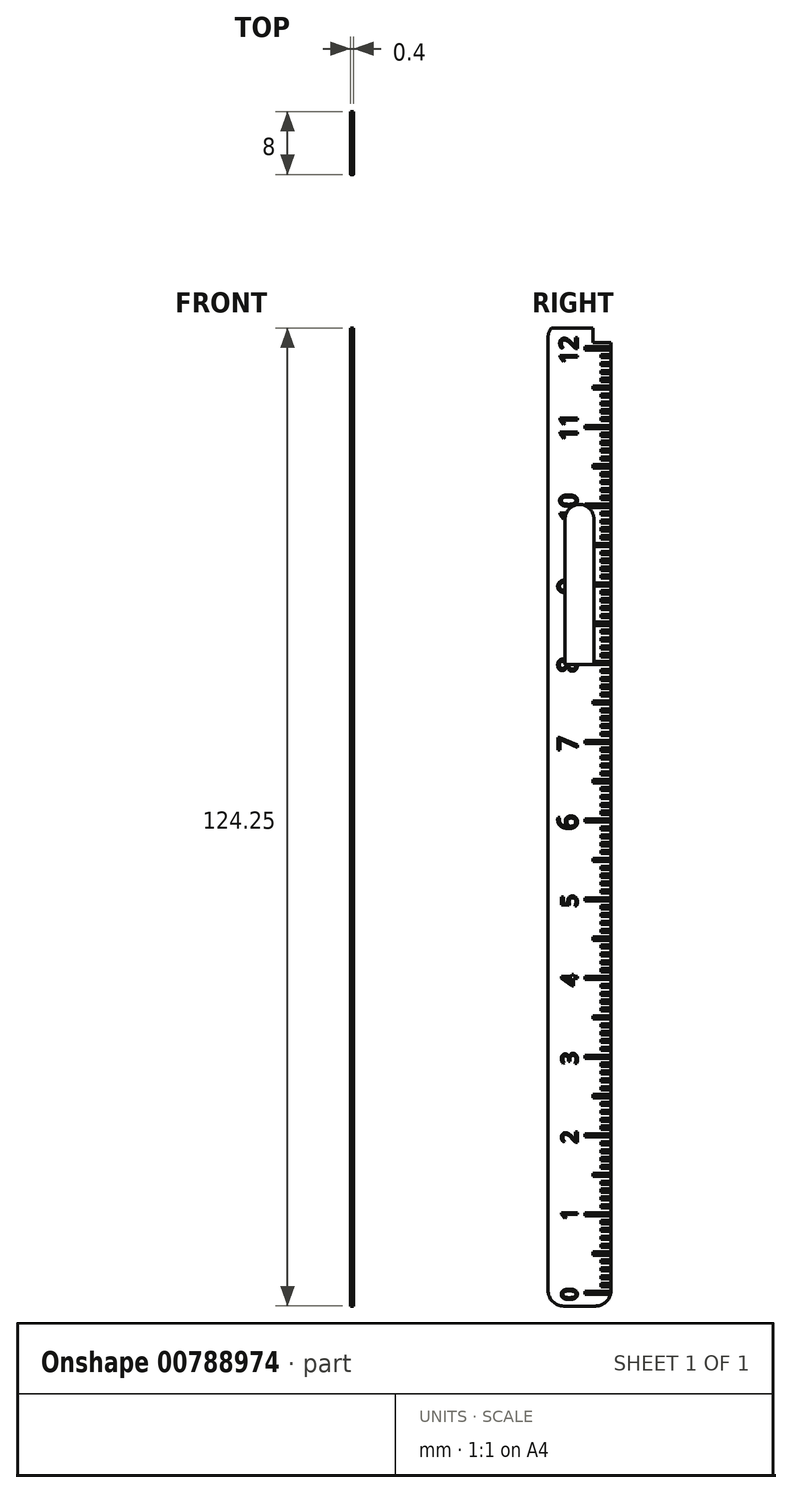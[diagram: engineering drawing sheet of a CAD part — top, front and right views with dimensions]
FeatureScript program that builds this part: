
annotation { "Feature Type Name" : "Feature", "Feature Type Description" : "" }
export const myFeature = defineFeature(function(context is Context, id is Id, definition is map)
    precondition{}
    {
        {
            var Q0;
            Q0=qCreatedBy(makeId("Right.planeOp"),FACE);
            var sketch = newSketch(context, id + "F0", { "sketchPlane" : qUnion([Q0])});
            skLineSegment(sketch, "E0.bottom", {"start": v(-20, 0) * mm, "end": v(-10, 0) * mm});
            skLineSegment(sketch, "E0.top", {"start": v(-20, 160) * mm, "end": v(-10, 160) * mm});
            skLineSegment(sketch, "E0.left", {"start": v(-20, 0) * mm, "end": v(-20, 160) * mm});
            skLineSegment(sketch, "E0.right", {"start": v(-10, 0) * mm, "end": v(-10, 160) * mm});
            skSolve(sketch);
        }
        {
            var Q0;
            Q0=qSketchRegion(id+"F0",true);
            extrude(context, id + "F1", {"entities" : qUnion([Q0]), "depth" : 0.1 * mm, "offsetDistance" : 25 * mm});
        }
        {
            var Q0;
            Q0=qCreatedBy(makeId("Right.planeOp"),FACE);
            var sketch = newSketch(context, id + "F2", { "sketchPlane" : qUnion([Q0])});
            skLineSegment(sketch, "E1", {"start": v(-12, 0) * mm, "end": v(-12, 150) * mm, "construction": true});
            skLineSegment(sketch, "E2", {"start": v(-14, 0) * mm, "end": v(-14, 150) * mm, "construction": true});
            skLineSegment(sketch, "E3", {"start": v(-13, 0) * mm, "end": v(-13, 150) * mm, "construction": true});
            skLineSegment(sketch, "E4.bottom", {"start": v(-14, 10.4) * mm, "end": v(-10, 10.4) * mm});
            skLineSegment(sketch, "E4.top", {"start": v(-14, 10) * mm, "end": v(-10, 10) * mm});
            skLineSegment(sketch, "E4.left", {"start": v(-14, 10) * mm, "end": v(-14, 10.4) * mm});
            skLineSegment(sketch, "E4.right", {"start": v(-10, 10) * mm, "end": v(-10, 10.4) * mm});
            skLineSegment(sketch, "E5.0.1.0", {"start": v(-14, 20.4) * mm, "end": v(-10, 20.4) * mm});
            skLineSegment(sketch, "E5.0.1.1", {"start": v(-14, 20) * mm, "end": v(-10, 20) * mm});
            skLineSegment(sketch, "E5.0.1.2", {"start": v(-14, 20) * mm, "end": v(-14, 20.4) * mm});
            skLineSegment(sketch, "E5.0.1.3", {"start": v(-10, 20) * mm, "end": v(-10, 20.4) * mm});
            skLineSegment(sketch, "E5.0.2.0", {"start": v(-14, 30.4) * mm, "end": v(-10, 30.4) * mm});
            skLineSegment(sketch, "E5.0.2.1", {"start": v(-14, 30) * mm, "end": v(-10, 30) * mm});
            skLineSegment(sketch, "E5.0.2.2", {"start": v(-14, 30) * mm, "end": v(-14, 30.4) * mm});
            skLineSegment(sketch, "E5.0.2.3", {"start": v(-10, 30) * mm, "end": v(-10, 30.4) * mm});
            skLineSegment(sketch, "E5.0.3.0", {"start": v(-14, 40.4) * mm, "end": v(-10, 40.4) * mm});
            skLineSegment(sketch, "E5.0.3.1", {"start": v(-14, 40) * mm, "end": v(-10, 40) * mm});
            skLineSegment(sketch, "E5.0.3.2", {"start": v(-14, 40) * mm, "end": v(-14, 40.4) * mm});
            skLineSegment(sketch, "E5.0.3.3", {"start": v(-10, 40) * mm, "end": v(-10, 40.4) * mm});
            skLineSegment(sketch, "E5.0.4.0", {"start": v(-14, 50.4) * mm, "end": v(-10, 50.4) * mm});
            skLineSegment(sketch, "E5.0.4.1", {"start": v(-14, 50) * mm, "end": v(-10, 50) * mm});
            skLineSegment(sketch, "E5.0.4.2", {"start": v(-14, 50) * mm, "end": v(-14, 50.4) * mm});
            skLineSegment(sketch, "E5.0.4.3", {"start": v(-10, 50) * mm, "end": v(-10, 50.4) * mm});
            skLineSegment(sketch, "E5.0.5.0", {"start": v(-14, 60.4) * mm, "end": v(-10, 60.4) * mm});
            skLineSegment(sketch, "E5.0.5.1", {"start": v(-14, 60) * mm, "end": v(-10, 60) * mm});
            skLineSegment(sketch, "E5.0.5.2", {"start": v(-14, 60) * mm, "end": v(-14, 60.4) * mm});
            skLineSegment(sketch, "E5.0.5.3", {"start": v(-10, 60) * mm, "end": v(-10, 60.4) * mm});
            skLineSegment(sketch, "E5.0.6.0", {"start": v(-14, 70.4) * mm, "end": v(-10, 70.4) * mm});
            skLineSegment(sketch, "E5.0.6.1", {"start": v(-14, 70) * mm, "end": v(-10, 70) * mm});
            skLineSegment(sketch, "E5.0.6.2", {"start": v(-14, 70) * mm, "end": v(-14, 70.4) * mm});
            skLineSegment(sketch, "E5.0.6.3", {"start": v(-10, 70) * mm, "end": v(-10, 70.4) * mm});
            skLineSegment(sketch, "E5.0.7.0", {"start": v(-14, 80.4) * mm, "end": v(-10, 80.4) * mm});
            skLineSegment(sketch, "E5.0.7.1", {"start": v(-14, 80) * mm, "end": v(-10, 80) * mm});
            skLineSegment(sketch, "E5.0.7.2", {"start": v(-14, 80) * mm, "end": v(-14, 80.4) * mm});
            skLineSegment(sketch, "E5.0.7.3", {"start": v(-10, 80) * mm, "end": v(-10, 80.4) * mm});
            skLineSegment(sketch, "E5.0.8.0", {"start": v(-14, 90.4) * mm, "end": v(-10, 90.4) * mm});
            skLineSegment(sketch, "E5.0.8.1", {"start": v(-14, 90) * mm, "end": v(-10, 90) * mm});
            skLineSegment(sketch, "E5.0.8.2", {"start": v(-14, 90) * mm, "end": v(-14, 90.4) * mm});
            skLineSegment(sketch, "E5.0.8.3", {"start": v(-10, 90) * mm, "end": v(-10, 90.4) * mm});
            skLineSegment(sketch, "E5.0.9.0", {"start": v(-14, 100.4) * mm, "end": v(-10, 100.4) * mm});
            skLineSegment(sketch, "E5.0.9.1", {"start": v(-14, 100) * mm, "end": v(-10, 100) * mm});
            skLineSegment(sketch, "E5.0.9.2", {"start": v(-14, 100) * mm, "end": v(-14, 100.4) * mm});
            skLineSegment(sketch, "E5.0.9.3", {"start": v(-10, 100) * mm, "end": v(-10, 100.4) * mm});
            skLineSegment(sketch, "E5.direction2", {"start": v(-14, 10) * mm, "end": v(-14, 20) * mm, "construction": true});
            skLineSegment(sketch, "E6.0.0.10", {"start": v(-14, 110.4) * mm, "end": v(-10, 110.4) * mm});
            skLineSegment(sketch, "E6.3.0.10", {"start": v(-14, 110) * mm, "end": v(-10, 110) * mm});
            skLineSegment(sketch, "E6.6.0.10", {"start": v(-14, 110) * mm, "end": v(-14, 110.4) * mm});
            skLineSegment(sketch, "E6.9.0.10", {"start": v(-10, 110) * mm, "end": v(-10, 110.4) * mm});
            skLineSegment(sketch, "E6.0.0.11", {"start": v(-14, 120.4) * mm, "end": v(-10, 120.4) * mm});
            skLineSegment(sketch, "E6.3.0.11", {"start": v(-14, 120) * mm, "end": v(-10, 120) * mm});
            skLineSegment(sketch, "E6.6.0.11", {"start": v(-14, 120) * mm, "end": v(-14, 120.4) * mm});
            skLineSegment(sketch, "E6.9.0.11", {"start": v(-10, 120) * mm, "end": v(-10, 120.4) * mm});
            skLineSegment(sketch, "E6.0.0.12", {"start": v(-14, 130.4) * mm, "end": v(-10, 130.4) * mm});
            skLineSegment(sketch, "E6.3.0.12", {"start": v(-14, 130) * mm, "end": v(-10, 130) * mm});
            skLineSegment(sketch, "E6.6.0.12", {"start": v(-14, 130) * mm, "end": v(-14, 130.4) * mm});
            skLineSegment(sketch, "E6.9.0.12", {"start": v(-10, 130) * mm, "end": v(-10, 130.4) * mm});
            skLineSegment(sketch, "E6.0.0.13", {"start": v(-14, 140.4) * mm, "end": v(-10, 140.4) * mm});
            skLineSegment(sketch, "E6.3.0.13", {"start": v(-14, 140) * mm, "end": v(-10, 140) * mm});
            skLineSegment(sketch, "E6.6.0.13", {"start": v(-14, 140) * mm, "end": v(-14, 140.4) * mm});
            skLineSegment(sketch, "E6.9.0.13", {"start": v(-10, 140) * mm, "end": v(-10, 140.4) * mm});
            skLineSegment(sketch, "E7.bottom", {"start": v(-10, 15) * mm, "end": v(-13, 15) * mm});
            skLineSegment(sketch, "E7.top", {"start": v(-10, 15.4) * mm, "end": v(-13, 15.4) * mm});
            skLineSegment(sketch, "E7.left", {"start": v(-10, 15) * mm, "end": v(-10, 15.4) * mm});
            skLineSegment(sketch, "E7.right", {"start": v(-13, 15) * mm, "end": v(-13, 15.4) * mm});
            skLineSegment(sketch, "E8", {"start": v(-22.56, 0) * mm, "end": v(-10, 0) * mm, "construction": true});
            skLineSegment(sketch, "E9", {"start": v(-15, 150) * mm, "end": v(-15, 0) * mm, "construction": true});
            skText(sketch, "E10", { "text": "0", "fontName": "OpenSans-Regular.ttf"});
            skText(sketch, "E11", { "text": "1\n", "fontName": "OpenSans-Regular.ttf"});
            skText(sketch, "E12", { "text": "2", "fontName": "OpenSans-Regular.ttf"});
            skText(sketch, "E13", { "text": "3", "fontName": "OpenSans-Regular.ttf"});
            skText(sketch, "E14", { "text": "4", "fontName": "OpenSans-Regular.ttf"});
            skText(sketch, "E15", { "text": "5", "fontName": "OpenSans-Regular.ttf"});
            skText(sketch, "E16", { "text": "6", "fontName": "OpenSans-Regular.ttf"});
            skText(sketch, "E17", { "text": "7", "fontName": "OpenSans-Regular.ttf"});
            skText(sketch, "E18", { "text": "8", "fontName": "OpenSans-Regular.ttf"});
            skText(sketch, "E19", { "text": "9", "fontName": "OpenSans-Regular.ttf"});
            skText(sketch, "E20", { "text": "10", "fontName": "OpenSans-Regular.ttf"});
            skText(sketch, "E21", { "text": "11", "fontName": "OpenSans-Regular.ttf"});
            skText(sketch, "E22", { "text": "12", "fontName": "OpenSans-Regular.ttf"});
            skText(sketch, "E23", { "text": "13", "fontName": "OpenSans-Regular.ttf"});
            skLineSegment(sketch, "E24.bottom", {"start": v(-12, 11) * mm, "end": v(-10, 11) * mm});
            skLineSegment(sketch, "E24.top", {"start": v(-12, 11.4) * mm, "end": v(-10, 11.4) * mm});
            skLineSegment(sketch, "E24.left", {"start": v(-12, 11) * mm, "end": v(-12, 11.4) * mm});
            skLineSegment(sketch, "E24.right", {"start": v(-10, 11) * mm, "end": v(-10, 11.4) * mm});
            skLineSegment(sketch, "E25.bottom", {"start": v(-12, 12) * mm, "end": v(-10, 12) * mm});
            skLineSegment(sketch, "E25.top", {"start": v(-12, 12.4) * mm, "end": v(-10, 12.4) * mm});
            skLineSegment(sketch, "E25.left", {"start": v(-12, 12) * mm, "end": v(-12, 12.4) * mm});
            skLineSegment(sketch, "E25.right", {"start": v(-10, 12) * mm, "end": v(-10, 12.4) * mm});
            skLineSegment(sketch, "E26.bottom", {"start": v(-12, 13) * mm, "end": v(-10, 13) * mm});
            skLineSegment(sketch, "E26.top", {"start": v(-12, 13.4) * mm, "end": v(-10, 13.4) * mm});
            skLineSegment(sketch, "E26.left", {"start": v(-12, 13) * mm, "end": v(-12, 13.4) * mm});
            skLineSegment(sketch, "E26.right", {"start": v(-10, 13) * mm, "end": v(-10, 13.4) * mm});
            skLineSegment(sketch, "E27.bottom", {"start": v(-12, 14) * mm, "end": v(-10, 14) * mm});
            skLineSegment(sketch, "E27.top", {"start": v(-12, 14.4) * mm, "end": v(-10, 14.4) * mm});
            skLineSegment(sketch, "E27.left", {"start": v(-12, 14) * mm, "end": v(-12, 14.4) * mm});
            skLineSegment(sketch, "E27.right", {"start": v(-10, 14) * mm, "end": v(-10, 14.4) * mm});
            skLineSegment(sketch, "E28.bottom", {"start": v(-12, 16) * mm, "end": v(-10, 16) * mm});
            skLineSegment(sketch, "E28.top", {"start": v(-12, 16.4) * mm, "end": v(-10, 16.4) * mm});
            skLineSegment(sketch, "E28.left", {"start": v(-12, 16) * mm, "end": v(-12, 16.4) * mm});
            skLineSegment(sketch, "E28.right", {"start": v(-10, 16) * mm, "end": v(-10, 16.4) * mm});
            skLineSegment(sketch, "E29.bottom", {"start": v(-12, 17) * mm, "end": v(-10, 17) * mm});
            skLineSegment(sketch, "E29.top", {"start": v(-12, 17.4) * mm, "end": v(-10, 17.4) * mm});
            skLineSegment(sketch, "E29.left", {"start": v(-12, 17) * mm, "end": v(-12, 17.4) * mm});
            skLineSegment(sketch, "E29.right", {"start": v(-10, 17) * mm, "end": v(-10, 17.4) * mm});
            skLineSegment(sketch, "E30.bottom", {"start": v(-12, 18) * mm, "end": v(-10, 18) * mm});
            skLineSegment(sketch, "E30.top", {"start": v(-12, 18.4) * mm, "end": v(-10, 18.4) * mm});
            skLineSegment(sketch, "E30.left", {"start": v(-12, 18) * mm, "end": v(-12, 18.4) * mm});
            skLineSegment(sketch, "E30.right", {"start": v(-10, 18) * mm, "end": v(-10, 18.4) * mm});
            skLineSegment(sketch, "E31.bottom", {"start": v(-12, 19) * mm, "end": v(-10, 19) * mm});
            skLineSegment(sketch, "E31.top", {"start": v(-12, 19.4) * mm, "end": v(-10, 19.4) * mm});
            skLineSegment(sketch, "E31.left", {"start": v(-12, 19) * mm, "end": v(-12, 19.4) * mm});
            skLineSegment(sketch, "E31.right", {"start": v(-10, 19) * mm, "end": v(-10, 19.4) * mm});
            skLineSegment(sketch, "E32.0.1.0", {"start": v(-12, 22) * mm, "end": v(-10, 22) * mm});
            skLineSegment(sketch, "E32.0.1.1", {"start": v(-12, 21.4) * mm, "end": v(-10, 21.4) * mm});
            skLineSegment(sketch, "E32.0.1.2", {"start": v(-12, 23.4) * mm, "end": v(-10, 23.4) * mm});
            skLineSegment(sketch, "E32.0.1.3", {"start": v(-12, 28.4) * mm, "end": v(-10, 28.4) * mm});
            skLineSegment(sketch, "E32.0.1.4", {"start": v(-12, 22.4) * mm, "end": v(-10, 22.4) * mm});
            skLineSegment(sketch, "E32.0.1.5", {"start": v(-12, 23) * mm, "end": v(-10, 23) * mm});
            skLineSegment(sketch, "E32.0.1.6", {"start": v(-10, 25.4) * mm, "end": v(-13, 25.4) * mm});
            skLineSegment(sketch, "E32.0.1.7", {"start": v(-12, 29) * mm, "end": v(-10, 29) * mm});
            skLineSegment(sketch, "E32.0.1.8", {"start": v(-12, 29.4) * mm, "end": v(-10, 29.4) * mm});
            skLineSegment(sketch, "E32.0.1.9", {"start": v(-12, 24.4) * mm, "end": v(-10, 24.4) * mm});
            skLineSegment(sketch, "E32.0.1.10", {"start": v(-12, 28) * mm, "end": v(-10, 28) * mm});
            skLineSegment(sketch, "E32.0.1.11", {"start": v(-12, 26) * mm, "end": v(-10, 26) * mm});
            skLineSegment(sketch, "E32.0.1.12", {"start": v(-12, 27) * mm, "end": v(-10, 27) * mm});
            skLineSegment(sketch, "E32.0.1.13", {"start": v(-12, 26.4) * mm, "end": v(-10, 26.4) * mm});
            skLineSegment(sketch, "E32.0.1.14", {"start": v(-12, 21) * mm, "end": v(-10, 21) * mm});
            skLineSegment(sketch, "E32.0.1.15", {"start": v(-10, 25) * mm, "end": v(-13, 25) * mm});
            skLineSegment(sketch, "E32.0.1.16", {"start": v(-12, 10) * mm, "end": v(-12, 160) * mm, "construction": true});
            skLineSegment(sketch, "E32.0.1.17", {"start": v(-13, 10) * mm, "end": v(-13, 160) * mm, "construction": true});
            skLineSegment(sketch, "E32.0.1.18", {"start": v(-12, 24) * mm, "end": v(-10, 24) * mm});
            skLineSegment(sketch, "E32.0.1.19", {"start": v(-12, 27.4) * mm, "end": v(-10, 27.4) * mm});
            skLineSegment(sketch, "E32.0.1.20", {"start": v(-12, 21) * mm, "end": v(-12, 21.4) * mm});
            skLineSegment(sketch, "E32.0.1.21", {"start": v(-10, 24) * mm, "end": v(-10, 24.4) * mm});
            skLineSegment(sketch, "E32.0.1.22", {"start": v(-10, 27) * mm, "end": v(-10, 27.4) * mm});
            skLineSegment(sketch, "E32.0.1.23", {"start": v(-12, 29) * mm, "end": v(-12, 29.4) * mm});
            skLineSegment(sketch, "E32.0.1.24", {"start": v(-10, 25) * mm, "end": v(-10, 25.4) * mm});
            skLineSegment(sketch, "E32.0.1.25", {"start": v(-12, 24) * mm, "end": v(-12, 24.4) * mm});
            skLineSegment(sketch, "E32.0.1.26", {"start": v(-12, 26) * mm, "end": v(-12, 26.4) * mm});
            skLineSegment(sketch, "E32.0.1.27", {"start": v(-10, 28) * mm, "end": v(-10, 28.4) * mm});
            skLineSegment(sketch, "E32.0.1.28", {"start": v(-12, 28) * mm, "end": v(-12, 28.4) * mm});
            skLineSegment(sketch, "E32.0.1.29", {"start": v(-10, 21) * mm, "end": v(-10, 21.4) * mm});
            skLineSegment(sketch, "E32.0.1.30", {"start": v(-10, 26) * mm, "end": v(-10, 26.4) * mm});
            skLineSegment(sketch, "E32.0.1.31", {"start": v(-10, 29) * mm, "end": v(-10, 29.4) * mm});
            skLineSegment(sketch, "E32.0.1.32", {"start": v(-12, 22) * mm, "end": v(-12, 22.4) * mm});
            skLineSegment(sketch, "E32.0.1.33", {"start": v(-10, 23) * mm, "end": v(-10, 23.4) * mm});
            skLineSegment(sketch, "E32.0.1.34", {"start": v(-13, 25) * mm, "end": v(-13, 25.4) * mm});
            skLineSegment(sketch, "E32.0.1.35", {"start": v(-10, 22) * mm, "end": v(-10, 22.4) * mm});
            skLineSegment(sketch, "E32.0.1.36", {"start": v(-12, 27) * mm, "end": v(-12, 27.4) * mm});
            skLineSegment(sketch, "E32.0.1.37", {"start": v(-12, 23) * mm, "end": v(-12, 23.4) * mm});
            skLineSegment(sketch, "E32.0.2.0", {"start": v(-12, 32) * mm, "end": v(-10, 32) * mm});
            skLineSegment(sketch, "E32.0.2.1", {"start": v(-12, 31.4) * mm, "end": v(-10, 31.4) * mm});
            skLineSegment(sketch, "E32.0.2.2", {"start": v(-12, 33.4) * mm, "end": v(-10, 33.4) * mm});
            skLineSegment(sketch, "E32.0.2.3", {"start": v(-12, 38.4) * mm, "end": v(-10, 38.4) * mm});
            skLineSegment(sketch, "E32.0.2.4", {"start": v(-12, 32.4) * mm, "end": v(-10, 32.4) * mm});
            skLineSegment(sketch, "E32.0.2.5", {"start": v(-12, 33) * mm, "end": v(-10, 33) * mm});
            skLineSegment(sketch, "E32.0.2.6", {"start": v(-10, 35.4) * mm, "end": v(-13, 35.4) * mm});
            skLineSegment(sketch, "E32.0.2.7", {"start": v(-12, 39) * mm, "end": v(-10, 39) * mm});
            skLineSegment(sketch, "E32.0.2.8", {"start": v(-12, 39.4) * mm, "end": v(-10, 39.4) * mm});
            skLineSegment(sketch, "E32.0.2.9", {"start": v(-12, 34.4) * mm, "end": v(-10, 34.4) * mm});
            skLineSegment(sketch, "E32.0.2.10", {"start": v(-12, 38) * mm, "end": v(-10, 38) * mm});
            skLineSegment(sketch, "E32.0.2.11", {"start": v(-12, 36) * mm, "end": v(-10, 36) * mm});
            skLineSegment(sketch, "E32.0.2.12", {"start": v(-12, 37) * mm, "end": v(-10, 37) * mm});
            skLineSegment(sketch, "E32.0.2.13", {"start": v(-12, 36.4) * mm, "end": v(-10, 36.4) * mm});
            skLineSegment(sketch, "E32.0.2.14", {"start": v(-12, 31) * mm, "end": v(-10, 31) * mm});
            skLineSegment(sketch, "E32.0.2.15", {"start": v(-10, 35) * mm, "end": v(-13, 35) * mm});
            skLineSegment(sketch, "E32.0.2.16", {"start": v(-12, 20) * mm, "end": v(-12, 170) * mm, "construction": true});
            skLineSegment(sketch, "E32.0.2.17", {"start": v(-13, 20) * mm, "end": v(-13, 170) * mm, "construction": true});
            skLineSegment(sketch, "E32.0.2.18", {"start": v(-12, 34) * mm, "end": v(-10, 34) * mm});
            skLineSegment(sketch, "E32.0.2.19", {"start": v(-12, 37.4) * mm, "end": v(-10, 37.4) * mm});
            skLineSegment(sketch, "E32.0.2.20", {"start": v(-12, 31) * mm, "end": v(-12, 31.4) * mm});
            skLineSegment(sketch, "E32.0.2.21", {"start": v(-10, 34) * mm, "end": v(-10, 34.4) * mm});
            skLineSegment(sketch, "E32.0.2.22", {"start": v(-10, 37) * mm, "end": v(-10, 37.4) * mm});
            skLineSegment(sketch, "E32.0.2.23", {"start": v(-12, 39) * mm, "end": v(-12, 39.4) * mm});
            skLineSegment(sketch, "E32.0.2.24", {"start": v(-10, 35) * mm, "end": v(-10, 35.4) * mm});
            skLineSegment(sketch, "E32.0.2.25", {"start": v(-12, 34) * mm, "end": v(-12, 34.4) * mm});
            skLineSegment(sketch, "E32.0.2.26", {"start": v(-12, 36) * mm, "end": v(-12, 36.4) * mm});
            skLineSegment(sketch, "E32.0.2.27", {"start": v(-10, 38) * mm, "end": v(-10, 38.4) * mm});
            skLineSegment(sketch, "E32.0.2.28", {"start": v(-12, 38) * mm, "end": v(-12, 38.4) * mm});
            skLineSegment(sketch, "E32.0.2.29", {"start": v(-10, 31) * mm, "end": v(-10, 31.4) * mm});
            skLineSegment(sketch, "E32.0.2.30", {"start": v(-10, 36) * mm, "end": v(-10, 36.4) * mm});
            skLineSegment(sketch, "E32.0.2.31", {"start": v(-10, 39) * mm, "end": v(-10, 39.4) * mm});
            skLineSegment(sketch, "E32.0.2.32", {"start": v(-12, 32) * mm, "end": v(-12, 32.4) * mm});
            skLineSegment(sketch, "E32.0.2.33", {"start": v(-10, 33) * mm, "end": v(-10, 33.4) * mm});
            skLineSegment(sketch, "E32.0.2.34", {"start": v(-13, 35) * mm, "end": v(-13, 35.4) * mm});
            skLineSegment(sketch, "E32.0.2.35", {"start": v(-10, 32) * mm, "end": v(-10, 32.4) * mm});
            skLineSegment(sketch, "E32.0.2.36", {"start": v(-12, 37) * mm, "end": v(-12, 37.4) * mm});
            skLineSegment(sketch, "E32.0.2.37", {"start": v(-12, 33) * mm, "end": v(-12, 33.4) * mm});
            skLineSegment(sketch, "E32.0.3.0", {"start": v(-12, 42) * mm, "end": v(-10, 42) * mm});
            skLineSegment(sketch, "E32.0.3.1", {"start": v(-12, 41.4) * mm, "end": v(-10, 41.4) * mm});
            skLineSegment(sketch, "E32.0.3.2", {"start": v(-12, 43.4) * mm, "end": v(-10, 43.4) * mm});
            skLineSegment(sketch, "E32.0.3.3", {"start": v(-12, 48.4) * mm, "end": v(-10, 48.4) * mm});
            skLineSegment(sketch, "E32.0.3.4", {"start": v(-12, 42.4) * mm, "end": v(-10, 42.4) * mm});
            skLineSegment(sketch, "E32.0.3.5", {"start": v(-12, 43) * mm, "end": v(-10, 43) * mm});
            skLineSegment(sketch, "E32.0.3.6", {"start": v(-10, 45.4) * mm, "end": v(-13, 45.4) * mm});
            skLineSegment(sketch, "E32.0.3.7", {"start": v(-12, 49) * mm, "end": v(-10, 49) * mm});
            skLineSegment(sketch, "E32.0.3.8", {"start": v(-12, 49.4) * mm, "end": v(-10, 49.4) * mm});
            skLineSegment(sketch, "E32.0.3.9", {"start": v(-12, 44.4) * mm, "end": v(-10, 44.4) * mm});
            skLineSegment(sketch, "E32.0.3.10", {"start": v(-12, 48) * mm, "end": v(-10, 48) * mm});
            skLineSegment(sketch, "E32.0.3.11", {"start": v(-12, 46) * mm, "end": v(-10, 46) * mm});
            skLineSegment(sketch, "E32.0.3.12", {"start": v(-12, 47) * mm, "end": v(-10, 47) * mm});
            skLineSegment(sketch, "E32.0.3.13", {"start": v(-12, 46.4) * mm, "end": v(-10, 46.4) * mm});
            skLineSegment(sketch, "E32.0.3.14", {"start": v(-12, 41) * mm, "end": v(-10, 41) * mm});
            skLineSegment(sketch, "E32.0.3.15", {"start": v(-10, 45) * mm, "end": v(-13, 45) * mm});
            skLineSegment(sketch, "E32.0.3.16", {"start": v(-12, 30) * mm, "end": v(-12, 180) * mm, "construction": true});
            skLineSegment(sketch, "E32.0.3.17", {"start": v(-13, 30) * mm, "end": v(-13, 180) * mm, "construction": true});
            skLineSegment(sketch, "E32.0.3.18", {"start": v(-12, 44) * mm, "end": v(-10, 44) * mm});
            skLineSegment(sketch, "E32.0.3.19", {"start": v(-12, 47.4) * mm, "end": v(-10, 47.4) * mm});
            skLineSegment(sketch, "E32.0.3.20", {"start": v(-12, 41) * mm, "end": v(-12, 41.4) * mm});
            skLineSegment(sketch, "E32.0.3.21", {"start": v(-10, 44) * mm, "end": v(-10, 44.4) * mm});
            skLineSegment(sketch, "E32.0.3.22", {"start": v(-10, 47) * mm, "end": v(-10, 47.4) * mm});
            skLineSegment(sketch, "E32.0.3.23", {"start": v(-12, 49) * mm, "end": v(-12, 49.4) * mm});
            skLineSegment(sketch, "E32.0.3.24", {"start": v(-10, 45) * mm, "end": v(-10, 45.4) * mm});
            skLineSegment(sketch, "E32.0.3.25", {"start": v(-12, 44) * mm, "end": v(-12, 44.4) * mm});
            skLineSegment(sketch, "E32.0.3.26", {"start": v(-12, 46) * mm, "end": v(-12, 46.4) * mm});
            skLineSegment(sketch, "E32.0.3.27", {"start": v(-10, 48) * mm, "end": v(-10, 48.4) * mm});
            skLineSegment(sketch, "E32.0.3.28", {"start": v(-12, 48) * mm, "end": v(-12, 48.4) * mm});
            skLineSegment(sketch, "E32.0.3.29", {"start": v(-10, 41) * mm, "end": v(-10, 41.4) * mm});
            skLineSegment(sketch, "E32.0.3.30", {"start": v(-10, 46) * mm, "end": v(-10, 46.4) * mm});
            skLineSegment(sketch, "E32.0.3.31", {"start": v(-10, 49) * mm, "end": v(-10, 49.4) * mm});
            skLineSegment(sketch, "E32.0.3.32", {"start": v(-12, 42) * mm, "end": v(-12, 42.4) * mm});
            skLineSegment(sketch, "E32.0.3.33", {"start": v(-10, 43) * mm, "end": v(-10, 43.4) * mm});
            skLineSegment(sketch, "E32.0.3.34", {"start": v(-13, 45) * mm, "end": v(-13, 45.4) * mm});
            skLineSegment(sketch, "E32.0.3.35", {"start": v(-10, 42) * mm, "end": v(-10, 42.4) * mm});
            skLineSegment(sketch, "E32.0.3.36", {"start": v(-12, 47) * mm, "end": v(-12, 47.4) * mm});
            skLineSegment(sketch, "E32.0.3.37", {"start": v(-12, 43) * mm, "end": v(-12, 43.4) * mm});
            skLineSegment(sketch, "E32.0.4.0", {"start": v(-12, 52) * mm, "end": v(-10, 52) * mm});
            skLineSegment(sketch, "E32.0.4.1", {"start": v(-12, 51.4) * mm, "end": v(-10, 51.4) * mm});
            skLineSegment(sketch, "E32.0.4.2", {"start": v(-12, 53.4) * mm, "end": v(-10, 53.4) * mm});
            skLineSegment(sketch, "E32.0.4.3", {"start": v(-12, 58.4) * mm, "end": v(-10, 58.4) * mm});
            skLineSegment(sketch, "E32.0.4.4", {"start": v(-12, 52.4) * mm, "end": v(-10, 52.4) * mm});
            skLineSegment(sketch, "E32.0.4.5", {"start": v(-12, 53) * mm, "end": v(-10, 53) * mm});
            skLineSegment(sketch, "E32.0.4.6", {"start": v(-10, 55.4) * mm, "end": v(-13, 55.4) * mm});
            skLineSegment(sketch, "E32.0.4.7", {"start": v(-12, 59) * mm, "end": v(-10, 59) * mm});
            skLineSegment(sketch, "E32.0.4.8", {"start": v(-12, 59.4) * mm, "end": v(-10, 59.4) * mm});
            skLineSegment(sketch, "E32.0.4.9", {"start": v(-12, 54.4) * mm, "end": v(-10, 54.4) * mm});
            skLineSegment(sketch, "E32.0.4.10", {"start": v(-12, 58) * mm, "end": v(-10, 58) * mm});
            skLineSegment(sketch, "E32.0.4.11", {"start": v(-12, 56) * mm, "end": v(-10, 56) * mm});
            skLineSegment(sketch, "E32.0.4.12", {"start": v(-12, 57) * mm, "end": v(-10, 57) * mm});
            skLineSegment(sketch, "E32.0.4.13", {"start": v(-12, 56.4) * mm, "end": v(-10, 56.4) * mm});
            skLineSegment(sketch, "E32.0.4.14", {"start": v(-12, 51) * mm, "end": v(-10, 51) * mm});
            skLineSegment(sketch, "E32.0.4.15", {"start": v(-10, 55) * mm, "end": v(-13, 55) * mm});
            skLineSegment(sketch, "E32.0.4.16", {"start": v(-12, 40) * mm, "end": v(-12, 190) * mm, "construction": true});
            skLineSegment(sketch, "E32.0.4.17", {"start": v(-13, 40) * mm, "end": v(-13, 190) * mm, "construction": true});
            skLineSegment(sketch, "E32.0.4.18", {"start": v(-12, 54) * mm, "end": v(-10, 54) * mm});
            skLineSegment(sketch, "E32.0.4.19", {"start": v(-12, 57.4) * mm, "end": v(-10, 57.4) * mm});
            skLineSegment(sketch, "E32.0.4.20", {"start": v(-12, 51) * mm, "end": v(-12, 51.4) * mm});
            skLineSegment(sketch, "E32.0.4.21", {"start": v(-10, 54) * mm, "end": v(-10, 54.4) * mm});
            skLineSegment(sketch, "E32.0.4.22", {"start": v(-10, 57) * mm, "end": v(-10, 57.4) * mm});
            skLineSegment(sketch, "E32.0.4.23", {"start": v(-12, 59) * mm, "end": v(-12, 59.4) * mm});
            skLineSegment(sketch, "E32.0.4.24", {"start": v(-10, 55) * mm, "end": v(-10, 55.4) * mm});
            skLineSegment(sketch, "E32.0.4.25", {"start": v(-12, 54) * mm, "end": v(-12, 54.4) * mm});
            skLineSegment(sketch, "E32.0.4.26", {"start": v(-12, 56) * mm, "end": v(-12, 56.4) * mm});
            skLineSegment(sketch, "E32.0.4.27", {"start": v(-10, 58) * mm, "end": v(-10, 58.4) * mm});
            skLineSegment(sketch, "E32.0.4.28", {"start": v(-12, 58) * mm, "end": v(-12, 58.4) * mm});
            skLineSegment(sketch, "E32.0.4.29", {"start": v(-10, 51) * mm, "end": v(-10, 51.4) * mm});
            skLineSegment(sketch, "E32.0.4.30", {"start": v(-10, 56) * mm, "end": v(-10, 56.4) * mm});
            skLineSegment(sketch, "E32.0.4.31", {"start": v(-10, 59) * mm, "end": v(-10, 59.4) * mm});
            skLineSegment(sketch, "E32.0.4.32", {"start": v(-12, 52) * mm, "end": v(-12, 52.4) * mm});
            skLineSegment(sketch, "E32.0.4.33", {"start": v(-10, 53) * mm, "end": v(-10, 53.4) * mm});
            skLineSegment(sketch, "E32.0.4.34", {"start": v(-13, 55) * mm, "end": v(-13, 55.4) * mm});
            skLineSegment(sketch, "E32.0.4.35", {"start": v(-10, 52) * mm, "end": v(-10, 52.4) * mm});
            skLineSegment(sketch, "E32.0.4.36", {"start": v(-12, 57) * mm, "end": v(-12, 57.4) * mm});
            skLineSegment(sketch, "E32.0.4.37", {"start": v(-12, 53) * mm, "end": v(-12, 53.4) * mm});
            skLineSegment(sketch, "E32.0.5.0", {"start": v(-12, 62) * mm, "end": v(-10, 62) * mm});
            skLineSegment(sketch, "E32.0.5.1", {"start": v(-12, 61.4) * mm, "end": v(-10, 61.4) * mm});
            skLineSegment(sketch, "E32.0.5.2", {"start": v(-12, 63.4) * mm, "end": v(-10, 63.4) * mm});
            skLineSegment(sketch, "E32.0.5.3", {"start": v(-12, 68.4) * mm, "end": v(-10, 68.4) * mm});
            skLineSegment(sketch, "E32.0.5.4", {"start": v(-12, 62.4) * mm, "end": v(-10, 62.4) * mm});
            skLineSegment(sketch, "E32.0.5.5", {"start": v(-12, 63) * mm, "end": v(-10, 63) * mm});
            skLineSegment(sketch, "E32.0.5.6", {"start": v(-10, 65.4) * mm, "end": v(-13, 65.4) * mm});
            skLineSegment(sketch, "E32.0.5.7", {"start": v(-12, 69) * mm, "end": v(-10, 69) * mm});
            skLineSegment(sketch, "E32.0.5.8", {"start": v(-12, 69.4) * mm, "end": v(-10, 69.4) * mm});
            skLineSegment(sketch, "E32.0.5.9", {"start": v(-12, 64.4) * mm, "end": v(-10, 64.4) * mm});
            skLineSegment(sketch, "E32.0.5.10", {"start": v(-12, 68) * mm, "end": v(-10, 68) * mm});
            skLineSegment(sketch, "E32.0.5.11", {"start": v(-12, 66) * mm, "end": v(-10, 66) * mm});
            skLineSegment(sketch, "E32.0.5.12", {"start": v(-12, 67) * mm, "end": v(-10, 67) * mm});
            skLineSegment(sketch, "E32.0.5.13", {"start": v(-12, 66.4) * mm, "end": v(-10, 66.4) * mm});
            skLineSegment(sketch, "E32.0.5.14", {"start": v(-12, 61) * mm, "end": v(-10, 61) * mm});
            skLineSegment(sketch, "E32.0.5.15", {"start": v(-10, 65) * mm, "end": v(-13, 65) * mm});
            skLineSegment(sketch, "E32.0.5.16", {"start": v(-12, 50) * mm, "end": v(-12, 200) * mm, "construction": true});
            skLineSegment(sketch, "E32.0.5.17", {"start": v(-13, 50) * mm, "end": v(-13, 200) * mm, "construction": true});
            skLineSegment(sketch, "E32.0.5.18", {"start": v(-12, 64) * mm, "end": v(-10, 64) * mm});
            skLineSegment(sketch, "E32.0.5.19", {"start": v(-12, 67.4) * mm, "end": v(-10, 67.4) * mm});
            skLineSegment(sketch, "E32.0.5.20", {"start": v(-12, 61) * mm, "end": v(-12, 61.4) * mm});
            skLineSegment(sketch, "E32.0.5.21", {"start": v(-10, 64) * mm, "end": v(-10, 64.4) * mm});
            skLineSegment(sketch, "E32.0.5.22", {"start": v(-10, 67) * mm, "end": v(-10, 67.4) * mm});
            skLineSegment(sketch, "E32.0.5.23", {"start": v(-12, 69) * mm, "end": v(-12, 69.4) * mm});
            skLineSegment(sketch, "E32.0.5.24", {"start": v(-10, 65) * mm, "end": v(-10, 65.4) * mm});
            skLineSegment(sketch, "E32.0.5.25", {"start": v(-12, 64) * mm, "end": v(-12, 64.4) * mm});
            skLineSegment(sketch, "E32.0.5.26", {"start": v(-12, 66) * mm, "end": v(-12, 66.4) * mm});
            skLineSegment(sketch, "E32.0.5.27", {"start": v(-10, 68) * mm, "end": v(-10, 68.4) * mm});
            skLineSegment(sketch, "E32.0.5.28", {"start": v(-12, 68) * mm, "end": v(-12, 68.4) * mm});
            skLineSegment(sketch, "E32.0.5.29", {"start": v(-10, 61) * mm, "end": v(-10, 61.4) * mm});
            skLineSegment(sketch, "E32.0.5.30", {"start": v(-10, 66) * mm, "end": v(-10, 66.4) * mm});
            skLineSegment(sketch, "E32.0.5.31", {"start": v(-10, 69) * mm, "end": v(-10, 69.4) * mm});
            skLineSegment(sketch, "E32.0.5.32", {"start": v(-12, 62) * mm, "end": v(-12, 62.4) * mm});
            skLineSegment(sketch, "E32.0.5.33", {"start": v(-10, 63) * mm, "end": v(-10, 63.4) * mm});
            skLineSegment(sketch, "E32.0.5.34", {"start": v(-13, 65) * mm, "end": v(-13, 65.4) * mm});
            skLineSegment(sketch, "E32.0.5.35", {"start": v(-10, 62) * mm, "end": v(-10, 62.4) * mm});
            skLineSegment(sketch, "E32.0.5.36", {"start": v(-12, 67) * mm, "end": v(-12, 67.4) * mm});
            skLineSegment(sketch, "E32.0.5.37", {"start": v(-12, 63) * mm, "end": v(-12, 63.4) * mm});
            skLineSegment(sketch, "E32.0.6.0", {"start": v(-12, 72) * mm, "end": v(-10, 72) * mm});
            skLineSegment(sketch, "E32.0.6.1", {"start": v(-12, 71.4) * mm, "end": v(-10, 71.4) * mm});
            skLineSegment(sketch, "E32.0.6.2", {"start": v(-12, 73.4) * mm, "end": v(-10, 73.4) * mm});
            skLineSegment(sketch, "E32.0.6.3", {"start": v(-12, 78.4) * mm, "end": v(-10, 78.4) * mm});
            skLineSegment(sketch, "E32.0.6.4", {"start": v(-12, 72.4) * mm, "end": v(-10, 72.4) * mm});
            skLineSegment(sketch, "E32.0.6.5", {"start": v(-12, 73) * mm, "end": v(-10, 73) * mm});
            skLineSegment(sketch, "E32.0.6.6", {"start": v(-10, 75.4) * mm, "end": v(-13, 75.4) * mm});
            skLineSegment(sketch, "E32.0.6.7", {"start": v(-12, 79) * mm, "end": v(-10, 79) * mm});
            skLineSegment(sketch, "E32.0.6.8", {"start": v(-12, 79.4) * mm, "end": v(-10, 79.4) * mm});
            skLineSegment(sketch, "E32.0.6.9", {"start": v(-12, 74.4) * mm, "end": v(-10, 74.4) * mm});
            skLineSegment(sketch, "E32.0.6.10", {"start": v(-12, 78) * mm, "end": v(-10, 78) * mm});
            skLineSegment(sketch, "E32.0.6.11", {"start": v(-12, 76) * mm, "end": v(-10, 76) * mm});
            skLineSegment(sketch, "E32.0.6.12", {"start": v(-12, 77) * mm, "end": v(-10, 77) * mm});
            skLineSegment(sketch, "E32.0.6.13", {"start": v(-12, 76.4) * mm, "end": v(-10, 76.4) * mm});
            skLineSegment(sketch, "E32.0.6.14", {"start": v(-12, 71) * mm, "end": v(-10, 71) * mm});
            skLineSegment(sketch, "E32.0.6.15", {"start": v(-10, 75) * mm, "end": v(-13, 75) * mm});
            skLineSegment(sketch, "E32.0.6.16", {"start": v(-12, 60) * mm, "end": v(-12, 210) * mm, "construction": true});
            skLineSegment(sketch, "E32.0.6.17", {"start": v(-13, 60) * mm, "end": v(-13, 210) * mm, "construction": true});
            skLineSegment(sketch, "E32.0.6.18", {"start": v(-12, 74) * mm, "end": v(-10, 74) * mm});
            skLineSegment(sketch, "E32.0.6.19", {"start": v(-12, 77.4) * mm, "end": v(-10, 77.4) * mm});
            skLineSegment(sketch, "E32.0.6.20", {"start": v(-12, 71) * mm, "end": v(-12, 71.4) * mm});
            skLineSegment(sketch, "E32.0.6.21", {"start": v(-10, 74) * mm, "end": v(-10, 74.4) * mm});
            skLineSegment(sketch, "E32.0.6.22", {"start": v(-10, 77) * mm, "end": v(-10, 77.4) * mm});
            skLineSegment(sketch, "E32.0.6.23", {"start": v(-12, 79) * mm, "end": v(-12, 79.4) * mm});
            skLineSegment(sketch, "E32.0.6.24", {"start": v(-10, 75) * mm, "end": v(-10, 75.4) * mm});
            skLineSegment(sketch, "E32.0.6.25", {"start": v(-12, 74) * mm, "end": v(-12, 74.4) * mm});
            skLineSegment(sketch, "E32.0.6.26", {"start": v(-12, 76) * mm, "end": v(-12, 76.4) * mm});
            skLineSegment(sketch, "E32.0.6.27", {"start": v(-10, 78) * mm, "end": v(-10, 78.4) * mm});
            skLineSegment(sketch, "E32.0.6.28", {"start": v(-12, 78) * mm, "end": v(-12, 78.4) * mm});
            skLineSegment(sketch, "E32.0.6.29", {"start": v(-10, 71) * mm, "end": v(-10, 71.4) * mm});
            skLineSegment(sketch, "E32.0.6.30", {"start": v(-10, 76) * mm, "end": v(-10, 76.4) * mm});
            skLineSegment(sketch, "E32.0.6.31", {"start": v(-10, 79) * mm, "end": v(-10, 79.4) * mm});
            skLineSegment(sketch, "E32.0.6.32", {"start": v(-12, 72) * mm, "end": v(-12, 72.4) * mm});
            skLineSegment(sketch, "E32.0.6.33", {"start": v(-10, 73) * mm, "end": v(-10, 73.4) * mm});
            skLineSegment(sketch, "E32.0.6.34", {"start": v(-13, 75) * mm, "end": v(-13, 75.4) * mm});
            skLineSegment(sketch, "E32.0.6.35", {"start": v(-10, 72) * mm, "end": v(-10, 72.4) * mm});
            skLineSegment(sketch, "E32.0.6.36", {"start": v(-12, 77) * mm, "end": v(-12, 77.4) * mm});
            skLineSegment(sketch, "E32.0.6.37", {"start": v(-12, 73) * mm, "end": v(-12, 73.4) * mm});
            skLineSegment(sketch, "E32.0.7.0", {"start": v(-12, 82) * mm, "end": v(-10, 82) * mm});
            skLineSegment(sketch, "E32.0.7.1", {"start": v(-12, 81.4) * mm, "end": v(-10, 81.4) * mm});
            skLineSegment(sketch, "E32.0.7.2", {"start": v(-12, 83.4) * mm, "end": v(-10, 83.4) * mm});
            skLineSegment(sketch, "E32.0.7.3", {"start": v(-12, 88.4) * mm, "end": v(-10, 88.4) * mm});
            skLineSegment(sketch, "E32.0.7.4", {"start": v(-12, 82.4) * mm, "end": v(-10, 82.4) * mm});
            skLineSegment(sketch, "E32.0.7.5", {"start": v(-12, 83) * mm, "end": v(-10, 83) * mm});
            skLineSegment(sketch, "E32.0.7.6", {"start": v(-10, 85.4) * mm, "end": v(-13, 85.4) * mm});
            skLineSegment(sketch, "E32.0.7.7", {"start": v(-12, 89) * mm, "end": v(-10, 89) * mm});
            skLineSegment(sketch, "E32.0.7.8", {"start": v(-12, 89.4) * mm, "end": v(-10, 89.4) * mm});
            skLineSegment(sketch, "E32.0.7.9", {"start": v(-12, 84.4) * mm, "end": v(-10, 84.4) * mm});
            skLineSegment(sketch, "E32.0.7.10", {"start": v(-12, 88) * mm, "end": v(-10, 88) * mm});
            skLineSegment(sketch, "E32.0.7.11", {"start": v(-12, 86) * mm, "end": v(-10, 86) * mm});
            skLineSegment(sketch, "E32.0.7.12", {"start": v(-12, 87) * mm, "end": v(-10, 87) * mm});
            skLineSegment(sketch, "E32.0.7.13", {"start": v(-12, 86.4) * mm, "end": v(-10, 86.4) * mm});
            skLineSegment(sketch, "E32.0.7.14", {"start": v(-12, 81) * mm, "end": v(-10, 81) * mm});
            skLineSegment(sketch, "E32.0.7.15", {"start": v(-10, 85) * mm, "end": v(-13, 85) * mm});
            skLineSegment(sketch, "E32.0.7.16", {"start": v(-12, 70) * mm, "end": v(-12, 220) * mm, "construction": true});
            skLineSegment(sketch, "E32.0.7.17", {"start": v(-13, 70) * mm, "end": v(-13, 220) * mm, "construction": true});
            skLineSegment(sketch, "E32.0.7.18", {"start": v(-12, 84) * mm, "end": v(-10, 84) * mm});
            skLineSegment(sketch, "E32.0.7.19", {"start": v(-12, 87.4) * mm, "end": v(-10, 87.4) * mm});
            skLineSegment(sketch, "E32.0.7.20", {"start": v(-12, 81) * mm, "end": v(-12, 81.4) * mm});
            skLineSegment(sketch, "E32.0.7.21", {"start": v(-10, 84) * mm, "end": v(-10, 84.4) * mm});
            skLineSegment(sketch, "E32.0.7.22", {"start": v(-10, 87) * mm, "end": v(-10, 87.4) * mm});
            skLineSegment(sketch, "E32.0.7.23", {"start": v(-12, 89) * mm, "end": v(-12, 89.4) * mm});
            skLineSegment(sketch, "E32.0.7.24", {"start": v(-10, 85) * mm, "end": v(-10, 85.4) * mm});
            skLineSegment(sketch, "E32.0.7.25", {"start": v(-12, 84) * mm, "end": v(-12, 84.4) * mm});
            skLineSegment(sketch, "E32.0.7.26", {"start": v(-12, 86) * mm, "end": v(-12, 86.4) * mm});
            skLineSegment(sketch, "E32.0.7.27", {"start": v(-10, 88) * mm, "end": v(-10, 88.4) * mm});
            skLineSegment(sketch, "E32.0.7.28", {"start": v(-12, 88) * mm, "end": v(-12, 88.4) * mm});
            skLineSegment(sketch, "E32.0.7.29", {"start": v(-10, 81) * mm, "end": v(-10, 81.4) * mm});
            skLineSegment(sketch, "E32.0.7.30", {"start": v(-10, 86) * mm, "end": v(-10, 86.4) * mm});
            skLineSegment(sketch, "E32.0.7.31", {"start": v(-10, 89) * mm, "end": v(-10, 89.4) * mm});
            skLineSegment(sketch, "E32.0.7.32", {"start": v(-12, 82) * mm, "end": v(-12, 82.4) * mm});
            skLineSegment(sketch, "E32.0.7.33", {"start": v(-10, 83) * mm, "end": v(-10, 83.4) * mm});
            skLineSegment(sketch, "E32.0.7.34", {"start": v(-13, 85) * mm, "end": v(-13, 85.4) * mm});
            skLineSegment(sketch, "E32.0.7.35", {"start": v(-10, 82) * mm, "end": v(-10, 82.4) * mm});
            skLineSegment(sketch, "E32.0.7.36", {"start": v(-12, 87) * mm, "end": v(-12, 87.4) * mm});
            skLineSegment(sketch, "E32.0.7.37", {"start": v(-12, 83) * mm, "end": v(-12, 83.4) * mm});
            skLineSegment(sketch, "E32.0.8.0", {"start": v(-12, 92) * mm, "end": v(-10, 92) * mm});
            skLineSegment(sketch, "E32.0.8.1", {"start": v(-12, 91.4) * mm, "end": v(-10, 91.4) * mm});
            skLineSegment(sketch, "E32.0.8.2", {"start": v(-12, 93.4) * mm, "end": v(-10, 93.4) * mm});
            skLineSegment(sketch, "E32.0.8.3", {"start": v(-12, 98.4) * mm, "end": v(-10, 98.4) * mm});
            skLineSegment(sketch, "E32.0.8.4", {"start": v(-12, 92.4) * mm, "end": v(-10, 92.4) * mm});
            skLineSegment(sketch, "E32.0.8.5", {"start": v(-12, 93) * mm, "end": v(-10, 93) * mm});
            skLineSegment(sketch, "E32.0.8.6", {"start": v(-10, 95.4) * mm, "end": v(-13, 95.4) * mm});
            skLineSegment(sketch, "E32.0.8.7", {"start": v(-12, 99) * mm, "end": v(-10, 99) * mm});
            skLineSegment(sketch, "E32.0.8.8", {"start": v(-12, 99.4) * mm, "end": v(-10, 99.4) * mm});
            skLineSegment(sketch, "E32.0.8.9", {"start": v(-12, 94.4) * mm, "end": v(-10, 94.4) * mm});
            skLineSegment(sketch, "E32.0.8.10", {"start": v(-12, 98) * mm, "end": v(-10, 98) * mm});
            skLineSegment(sketch, "E32.0.8.11", {"start": v(-12, 96) * mm, "end": v(-10, 96) * mm});
            skLineSegment(sketch, "E32.0.8.12", {"start": v(-12, 97) * mm, "end": v(-10, 97) * mm});
            skLineSegment(sketch, "E32.0.8.13", {"start": v(-12, 96.4) * mm, "end": v(-10, 96.4) * mm});
            skLineSegment(sketch, "E32.0.8.14", {"start": v(-12, 91) * mm, "end": v(-10, 91) * mm});
            skLineSegment(sketch, "E32.0.8.15", {"start": v(-10, 95) * mm, "end": v(-13, 95) * mm});
            skLineSegment(sketch, "E32.0.8.16", {"start": v(-12, 80) * mm, "end": v(-12, 230) * mm, "construction": true});
            skLineSegment(sketch, "E32.0.8.17", {"start": v(-13, 80) * mm, "end": v(-13, 230) * mm, "construction": true});
            skLineSegment(sketch, "E32.0.8.18", {"start": v(-12, 94) * mm, "end": v(-10, 94) * mm});
            skLineSegment(sketch, "E32.0.8.19", {"start": v(-12, 97.4) * mm, "end": v(-10, 97.4) * mm});
            skLineSegment(sketch, "E32.0.8.20", {"start": v(-12, 91) * mm, "end": v(-12, 91.4) * mm});
            skLineSegment(sketch, "E32.0.8.21", {"start": v(-10, 94) * mm, "end": v(-10, 94.4) * mm});
            skLineSegment(sketch, "E32.0.8.22", {"start": v(-10, 97) * mm, "end": v(-10, 97.4) * mm});
            skLineSegment(sketch, "E32.0.8.23", {"start": v(-12, 99) * mm, "end": v(-12, 99.4) * mm});
            skLineSegment(sketch, "E32.0.8.24", {"start": v(-10, 95) * mm, "end": v(-10, 95.4) * mm});
            skLineSegment(sketch, "E32.0.8.25", {"start": v(-12, 94) * mm, "end": v(-12, 94.4) * mm});
            skLineSegment(sketch, "E32.0.8.26", {"start": v(-12, 96) * mm, "end": v(-12, 96.4) * mm});
            skLineSegment(sketch, "E32.0.8.27", {"start": v(-10, 98) * mm, "end": v(-10, 98.4) * mm});
            skLineSegment(sketch, "E32.0.8.28", {"start": v(-12, 98) * mm, "end": v(-12, 98.4) * mm});
            skLineSegment(sketch, "E32.0.8.29", {"start": v(-10, 91) * mm, "end": v(-10, 91.4) * mm});
            skLineSegment(sketch, "E32.0.8.30", {"start": v(-10, 96) * mm, "end": v(-10, 96.4) * mm});
            skLineSegment(sketch, "E32.0.8.31", {"start": v(-10, 99) * mm, "end": v(-10, 99.4) * mm});
            skLineSegment(sketch, "E32.0.8.32", {"start": v(-12, 92) * mm, "end": v(-12, 92.4) * mm});
            skLineSegment(sketch, "E32.0.8.33", {"start": v(-10, 93) * mm, "end": v(-10, 93.4) * mm});
            skLineSegment(sketch, "E32.0.8.34", {"start": v(-13, 95) * mm, "end": v(-13, 95.4) * mm});
            skLineSegment(sketch, "E32.0.8.35", {"start": v(-10, 92) * mm, "end": v(-10, 92.4) * mm});
            skLineSegment(sketch, "E32.0.8.36", {"start": v(-12, 97) * mm, "end": v(-12, 97.4) * mm});
            skLineSegment(sketch, "E32.0.8.37", {"start": v(-12, 93) * mm, "end": v(-12, 93.4) * mm});
            skLineSegment(sketch, "E32.0.9.0", {"start": v(-12, 102) * mm, "end": v(-10, 102) * mm});
            skLineSegment(sketch, "E32.0.9.1", {"start": v(-12, 101.4) * mm, "end": v(-10, 101.4) * mm});
            skLineSegment(sketch, "E32.0.9.2", {"start": v(-12, 103.4) * mm, "end": v(-10, 103.4) * mm});
            skLineSegment(sketch, "E32.0.9.3", {"start": v(-12, 108.4) * mm, "end": v(-10, 108.4) * mm});
            skLineSegment(sketch, "E32.0.9.4", {"start": v(-12, 102.4) * mm, "end": v(-10, 102.4) * mm});
            skLineSegment(sketch, "E32.0.9.5", {"start": v(-12, 103) * mm, "end": v(-10, 103) * mm});
            skLineSegment(sketch, "E32.0.9.6", {"start": v(-10, 105.4) * mm, "end": v(-13, 105.4) * mm});
            skLineSegment(sketch, "E32.0.9.7", {"start": v(-12, 109) * mm, "end": v(-10, 109) * mm});
            skLineSegment(sketch, "E32.0.9.8", {"start": v(-12, 109.4) * mm, "end": v(-10, 109.4) * mm});
            skLineSegment(sketch, "E32.0.9.9", {"start": v(-12, 104.4) * mm, "end": v(-10, 104.4) * mm});
            skLineSegment(sketch, "E32.0.9.10", {"start": v(-12, 108) * mm, "end": v(-10, 108) * mm});
            skLineSegment(sketch, "E32.0.9.11", {"start": v(-12, 106) * mm, "end": v(-10, 106) * mm});
            skLineSegment(sketch, "E32.0.9.12", {"start": v(-12, 107) * mm, "end": v(-10, 107) * mm});
            skLineSegment(sketch, "E32.0.9.13", {"start": v(-12, 106.4) * mm, "end": v(-10, 106.4) * mm});
            skLineSegment(sketch, "E32.0.9.14", {"start": v(-12, 101) * mm, "end": v(-10, 101) * mm});
            skLineSegment(sketch, "E32.0.9.15", {"start": v(-10, 105) * mm, "end": v(-13, 105) * mm});
            skLineSegment(sketch, "E32.0.9.16", {"start": v(-12, 90) * mm, "end": v(-12, 240) * mm, "construction": true});
            skLineSegment(sketch, "E32.0.9.17", {"start": v(-13, 90) * mm, "end": v(-13, 240) * mm, "construction": true});
            skLineSegment(sketch, "E32.0.9.18", {"start": v(-12, 104) * mm, "end": v(-10, 104) * mm});
            skLineSegment(sketch, "E32.0.9.19", {"start": v(-12, 107.4) * mm, "end": v(-10, 107.4) * mm});
            skLineSegment(sketch, "E32.0.9.20", {"start": v(-12, 101) * mm, "end": v(-12, 101.4) * mm});
            skLineSegment(sketch, "E32.0.9.21", {"start": v(-10, 104) * mm, "end": v(-10, 104.4) * mm});
            skLineSegment(sketch, "E32.0.9.22", {"start": v(-10, 107) * mm, "end": v(-10, 107.4) * mm});
            skLineSegment(sketch, "E32.0.9.23", {"start": v(-12, 109) * mm, "end": v(-12, 109.4) * mm});
            skLineSegment(sketch, "E32.0.9.24", {"start": v(-10, 105) * mm, "end": v(-10, 105.4) * mm});
            skLineSegment(sketch, "E32.0.9.25", {"start": v(-12, 104) * mm, "end": v(-12, 104.4) * mm});
            skLineSegment(sketch, "E32.0.9.26", {"start": v(-12, 106) * mm, "end": v(-12, 106.4) * mm});
            skLineSegment(sketch, "E32.0.9.27", {"start": v(-10, 108) * mm, "end": v(-10, 108.4) * mm});
            skLineSegment(sketch, "E32.0.9.28", {"start": v(-12, 108) * mm, "end": v(-12, 108.4) * mm});
            skLineSegment(sketch, "E32.0.9.29", {"start": v(-10, 101) * mm, "end": v(-10, 101.4) * mm});
            skLineSegment(sketch, "E32.0.9.30", {"start": v(-10, 106) * mm, "end": v(-10, 106.4) * mm});
            skLineSegment(sketch, "E32.0.9.31", {"start": v(-10, 109) * mm, "end": v(-10, 109.4) * mm});
            skLineSegment(sketch, "E32.0.9.32", {"start": v(-12, 102) * mm, "end": v(-12, 102.4) * mm});
            skLineSegment(sketch, "E32.0.9.33", {"start": v(-10, 103) * mm, "end": v(-10, 103.4) * mm});
            skLineSegment(sketch, "E32.0.9.34", {"start": v(-13, 105) * mm, "end": v(-13, 105.4) * mm});
            skLineSegment(sketch, "E32.0.9.35", {"start": v(-10, 102) * mm, "end": v(-10, 102.4) * mm});
            skLineSegment(sketch, "E32.0.9.36", {"start": v(-12, 107) * mm, "end": v(-12, 107.4) * mm});
            skLineSegment(sketch, "E32.0.9.37", {"start": v(-12, 103) * mm, "end": v(-12, 103.4) * mm});
            skLineSegment(sketch, "E32.0.10.0", {"start": v(-12, 112) * mm, "end": v(-10, 112) * mm});
            skLineSegment(sketch, "E32.0.10.1", {"start": v(-12, 111.4) * mm, "end": v(-10, 111.4) * mm});
            skLineSegment(sketch, "E32.0.10.2", {"start": v(-12, 113.4) * mm, "end": v(-10, 113.4) * mm});
            skLineSegment(sketch, "E32.0.10.3", {"start": v(-12, 118.4) * mm, "end": v(-10, 118.4) * mm});
            skLineSegment(sketch, "E32.0.10.4", {"start": v(-12, 112.4) * mm, "end": v(-10, 112.4) * mm});
            skLineSegment(sketch, "E32.0.10.5", {"start": v(-12, 113) * mm, "end": v(-10, 113) * mm});
            skLineSegment(sketch, "E32.0.10.6", {"start": v(-10, 115.4) * mm, "end": v(-13, 115.4) * mm});
            skLineSegment(sketch, "E32.0.10.7", {"start": v(-12, 119) * mm, "end": v(-10, 119) * mm});
            skLineSegment(sketch, "E32.0.10.8", {"start": v(-12, 119.4) * mm, "end": v(-10, 119.4) * mm});
            skLineSegment(sketch, "E32.0.10.9", {"start": v(-12, 114.4) * mm, "end": v(-10, 114.4) * mm});
            skLineSegment(sketch, "E32.0.10.10", {"start": v(-12, 118) * mm, "end": v(-10, 118) * mm});
            skLineSegment(sketch, "E32.0.10.11", {"start": v(-12, 116) * mm, "end": v(-10, 116) * mm});
            skLineSegment(sketch, "E32.0.10.12", {"start": v(-12, 117) * mm, "end": v(-10, 117) * mm});
            skLineSegment(sketch, "E32.0.10.13", {"start": v(-12, 116.4) * mm, "end": v(-10, 116.4) * mm});
            skLineSegment(sketch, "E32.0.10.14", {"start": v(-12, 111) * mm, "end": v(-10, 111) * mm});
            skLineSegment(sketch, "E32.0.10.15", {"start": v(-10, 115) * mm, "end": v(-13, 115) * mm});
            skLineSegment(sketch, "E32.0.10.16", {"start": v(-12, 100) * mm, "end": v(-12, 250) * mm, "construction": true});
            skLineSegment(sketch, "E32.0.10.17", {"start": v(-13, 100) * mm, "end": v(-13, 250) * mm, "construction": true});
            skLineSegment(sketch, "E32.0.10.18", {"start": v(-12, 114) * mm, "end": v(-10, 114) * mm});
            skLineSegment(sketch, "E32.0.10.19", {"start": v(-12, 117.4) * mm, "end": v(-10, 117.4) * mm});
            skLineSegment(sketch, "E32.0.10.20", {"start": v(-12, 111) * mm, "end": v(-12, 111.4) * mm});
            skLineSegment(sketch, "E32.0.10.21", {"start": v(-10, 114) * mm, "end": v(-10, 114.4) * mm});
            skLineSegment(sketch, "E32.0.10.22", {"start": v(-10, 117) * mm, "end": v(-10, 117.4) * mm});
            skLineSegment(sketch, "E32.0.10.23", {"start": v(-12, 119) * mm, "end": v(-12, 119.4) * mm});
            skLineSegment(sketch, "E32.0.10.24", {"start": v(-10, 115) * mm, "end": v(-10, 115.4) * mm});
            skLineSegment(sketch, "E32.0.10.25", {"start": v(-12, 114) * mm, "end": v(-12, 114.4) * mm});
            skLineSegment(sketch, "E32.0.10.26", {"start": v(-12, 116) * mm, "end": v(-12, 116.4) * mm});
            skLineSegment(sketch, "E32.0.10.27", {"start": v(-10, 118) * mm, "end": v(-10, 118.4) * mm});
            skLineSegment(sketch, "E32.0.10.28", {"start": v(-12, 118) * mm, "end": v(-12, 118.4) * mm});
            skLineSegment(sketch, "E32.0.10.29", {"start": v(-10, 111) * mm, "end": v(-10, 111.4) * mm});
            skLineSegment(sketch, "E32.0.10.30", {"start": v(-10, 116) * mm, "end": v(-10, 116.4) * mm});
            skLineSegment(sketch, "E32.0.10.31", {"start": v(-10, 119) * mm, "end": v(-10, 119.4) * mm});
            skLineSegment(sketch, "E32.0.10.32", {"start": v(-12, 112) * mm, "end": v(-12, 112.4) * mm});
            skLineSegment(sketch, "E32.0.10.33", {"start": v(-10, 113) * mm, "end": v(-10, 113.4) * mm});
            skLineSegment(sketch, "E32.0.10.34", {"start": v(-13, 115) * mm, "end": v(-13, 115.4) * mm});
            skLineSegment(sketch, "E32.0.10.35", {"start": v(-10, 112) * mm, "end": v(-10, 112.4) * mm});
            skLineSegment(sketch, "E32.0.10.36", {"start": v(-12, 117) * mm, "end": v(-12, 117.4) * mm});
            skLineSegment(sketch, "E32.0.10.37", {"start": v(-12, 113) * mm, "end": v(-12, 113.4) * mm});
            skLineSegment(sketch, "E32.0.11.0", {"start": v(-12, 122) * mm, "end": v(-10, 122) * mm});
            skLineSegment(sketch, "E32.0.11.1", {"start": v(-12, 121.4) * mm, "end": v(-10, 121.4) * mm});
            skLineSegment(sketch, "E32.0.11.2", {"start": v(-12, 123.4) * mm, "end": v(-10, 123.4) * mm});
            skLineSegment(sketch, "E32.0.11.3", {"start": v(-12, 128.4) * mm, "end": v(-10, 128.4) * mm});
            skLineSegment(sketch, "E32.0.11.4", {"start": v(-12, 122.4) * mm, "end": v(-10, 122.4) * mm});
            skLineSegment(sketch, "E32.0.11.5", {"start": v(-12, 123) * mm, "end": v(-10, 123) * mm});
            skLineSegment(sketch, "E32.0.11.6", {"start": v(-10, 125.4) * mm, "end": v(-13, 125.4) * mm});
            skLineSegment(sketch, "E32.0.11.7", {"start": v(-12, 129) * mm, "end": v(-10, 129) * mm});
            skLineSegment(sketch, "E32.0.11.8", {"start": v(-12, 129.4) * mm, "end": v(-10, 129.4) * mm});
            skLineSegment(sketch, "E32.0.11.9", {"start": v(-12, 124.4) * mm, "end": v(-10, 124.4) * mm});
            skLineSegment(sketch, "E32.0.11.10", {"start": v(-12, 128) * mm, "end": v(-10, 128) * mm});
            skLineSegment(sketch, "E32.0.11.11", {"start": v(-12, 126) * mm, "end": v(-10, 126) * mm});
            skLineSegment(sketch, "E32.0.11.12", {"start": v(-12, 127) * mm, "end": v(-10, 127) * mm});
            skLineSegment(sketch, "E32.0.11.13", {"start": v(-12, 126.4) * mm, "end": v(-10, 126.4) * mm});
            skLineSegment(sketch, "E32.0.11.14", {"start": v(-12, 121) * mm, "end": v(-10, 121) * mm});
            skLineSegment(sketch, "E32.0.11.15", {"start": v(-10, 125) * mm, "end": v(-13, 125) * mm});
            skLineSegment(sketch, "E32.0.11.16", {"start": v(-12, 110) * mm, "end": v(-12, 260) * mm, "construction": true});
            skLineSegment(sketch, "E32.0.11.17", {"start": v(-13, 110) * mm, "end": v(-13, 260) * mm, "construction": true});
            skLineSegment(sketch, "E32.0.11.18", {"start": v(-12, 124) * mm, "end": v(-10, 124) * mm});
            skLineSegment(sketch, "E32.0.11.19", {"start": v(-12, 127.4) * mm, "end": v(-10, 127.4) * mm});
            skLineSegment(sketch, "E32.0.11.20", {"start": v(-12, 121) * mm, "end": v(-12, 121.4) * mm});
            skLineSegment(sketch, "E32.0.11.21", {"start": v(-10, 124) * mm, "end": v(-10, 124.4) * mm});
            skLineSegment(sketch, "E32.0.11.22", {"start": v(-10, 127) * mm, "end": v(-10, 127.4) * mm});
            skLineSegment(sketch, "E32.0.11.23", {"start": v(-12, 129) * mm, "end": v(-12, 129.4) * mm});
            skLineSegment(sketch, "E32.0.11.24", {"start": v(-10, 125) * mm, "end": v(-10, 125.4) * mm});
            skLineSegment(sketch, "E32.0.11.25", {"start": v(-12, 124) * mm, "end": v(-12, 124.4) * mm});
            skLineSegment(sketch, "E32.0.11.26", {"start": v(-12, 126) * mm, "end": v(-12, 126.4) * mm});
            skLineSegment(sketch, "E32.0.11.27", {"start": v(-10, 128) * mm, "end": v(-10, 128.4) * mm});
            skLineSegment(sketch, "E32.0.11.28", {"start": v(-12, 128) * mm, "end": v(-12, 128.4) * mm});
            skLineSegment(sketch, "E32.0.11.29", {"start": v(-10, 121) * mm, "end": v(-10, 121.4) * mm});
            skLineSegment(sketch, "E32.0.11.30", {"start": v(-10, 126) * mm, "end": v(-10, 126.4) * mm});
            skLineSegment(sketch, "E32.0.11.31", {"start": v(-10, 129) * mm, "end": v(-10, 129.4) * mm});
            skLineSegment(sketch, "E32.0.11.32", {"start": v(-12, 122) * mm, "end": v(-12, 122.4) * mm});
            skLineSegment(sketch, "E32.0.11.33", {"start": v(-10, 123) * mm, "end": v(-10, 123.4) * mm});
            skLineSegment(sketch, "E32.0.11.34", {"start": v(-13, 125) * mm, "end": v(-13, 125.4) * mm});
            skLineSegment(sketch, "E32.0.11.35", {"start": v(-10, 122) * mm, "end": v(-10, 122.4) * mm});
            skLineSegment(sketch, "E32.0.11.36", {"start": v(-12, 127) * mm, "end": v(-12, 127.4) * mm});
            skLineSegment(sketch, "E32.0.11.37", {"start": v(-12, 123) * mm, "end": v(-12, 123.4) * mm});
            skLineSegment(sketch, "E32.0.12.0", {"start": v(-12, 132) * mm, "end": v(-10, 132) * mm});
            skLineSegment(sketch, "E32.0.12.1", {"start": v(-12, 131.4) * mm, "end": v(-10, 131.4) * mm});
            skLineSegment(sketch, "E32.0.12.2", {"start": v(-12, 133.4) * mm, "end": v(-10, 133.4) * mm});
            skLineSegment(sketch, "E32.0.12.3", {"start": v(-12, 138.4) * mm, "end": v(-10, 138.4) * mm});
            skLineSegment(sketch, "E32.0.12.4", {"start": v(-12, 132.4) * mm, "end": v(-10, 132.4) * mm});
            skLineSegment(sketch, "E32.0.12.5", {"start": v(-12, 133) * mm, "end": v(-10, 133) * mm});
            skLineSegment(sketch, "E32.0.12.6", {"start": v(-10, 135.4) * mm, "end": v(-13, 135.4) * mm});
            skLineSegment(sketch, "E32.0.12.7", {"start": v(-12, 139) * mm, "end": v(-10, 139) * mm});
            skLineSegment(sketch, "E32.0.12.8", {"start": v(-12, 139.4) * mm, "end": v(-10, 139.4) * mm});
            skLineSegment(sketch, "E32.0.12.9", {"start": v(-12, 134.4) * mm, "end": v(-10, 134.4) * mm});
            skLineSegment(sketch, "E32.0.12.10", {"start": v(-12, 138) * mm, "end": v(-10, 138) * mm});
            skLineSegment(sketch, "E32.0.12.11", {"start": v(-12, 136) * mm, "end": v(-10, 136) * mm});
            skLineSegment(sketch, "E32.0.12.12", {"start": v(-12, 137) * mm, "end": v(-10, 137) * mm});
            skLineSegment(sketch, "E32.0.12.13", {"start": v(-12, 136.4) * mm, "end": v(-10, 136.4) * mm});
            skLineSegment(sketch, "E32.0.12.14", {"start": v(-12, 131) * mm, "end": v(-10, 131) * mm});
            skLineSegment(sketch, "E32.0.12.15", {"start": v(-10, 135) * mm, "end": v(-13, 135) * mm});
            skLineSegment(sketch, "E32.0.12.16", {"start": v(-12, 120) * mm, "end": v(-12, 270) * mm, "construction": true});
            skLineSegment(sketch, "E32.0.12.17", {"start": v(-13, 120) * mm, "end": v(-13, 270) * mm, "construction": true});
            skLineSegment(sketch, "E32.0.12.18", {"start": v(-12, 134) * mm, "end": v(-10, 134) * mm});
            skLineSegment(sketch, "E32.0.12.19", {"start": v(-12, 137.4) * mm, "end": v(-10, 137.4) * mm});
            skLineSegment(sketch, "E32.0.12.20", {"start": v(-12, 131) * mm, "end": v(-12, 131.4) * mm});
            skLineSegment(sketch, "E32.0.12.21", {"start": v(-10, 134) * mm, "end": v(-10, 134.4) * mm});
            skLineSegment(sketch, "E32.0.12.22", {"start": v(-10, 137) * mm, "end": v(-10, 137.4) * mm});
            skLineSegment(sketch, "E32.0.12.23", {"start": v(-12, 139) * mm, "end": v(-12, 139.4) * mm});
            skLineSegment(sketch, "E32.0.12.24", {"start": v(-10, 135) * mm, "end": v(-10, 135.4) * mm});
            skLineSegment(sketch, "E32.0.12.25", {"start": v(-12, 134) * mm, "end": v(-12, 134.4) * mm});
            skLineSegment(sketch, "E32.0.12.26", {"start": v(-12, 136) * mm, "end": v(-12, 136.4) * mm});
            skLineSegment(sketch, "E32.0.12.27", {"start": v(-10, 138) * mm, "end": v(-10, 138.4) * mm});
            skLineSegment(sketch, "E32.0.12.28", {"start": v(-12, 138) * mm, "end": v(-12, 138.4) * mm});
            skLineSegment(sketch, "E32.0.12.29", {"start": v(-10, 131) * mm, "end": v(-10, 131.4) * mm});
            skLineSegment(sketch, "E32.0.12.30", {"start": v(-10, 136) * mm, "end": v(-10, 136.4) * mm});
            skLineSegment(sketch, "E32.0.12.31", {"start": v(-10, 139) * mm, "end": v(-10, 139.4) * mm});
            skLineSegment(sketch, "E32.0.12.32", {"start": v(-12, 132) * mm, "end": v(-12, 132.4) * mm});
            skLineSegment(sketch, "E32.0.12.33", {"start": v(-10, 133) * mm, "end": v(-10, 133.4) * mm});
            skLineSegment(sketch, "E32.0.12.34", {"start": v(-13, 135) * mm, "end": v(-13, 135.4) * mm});
            skLineSegment(sketch, "E32.0.12.35", {"start": v(-10, 132) * mm, "end": v(-10, 132.4) * mm});
            skLineSegment(sketch, "E32.0.12.36", {"start": v(-12, 137) * mm, "end": v(-12, 137.4) * mm});
            skLineSegment(sketch, "E32.0.12.37", {"start": v(-12, 133) * mm, "end": v(-12, 133.4) * mm});
            skLineSegment(sketch, "E32.direction1", {"start": v(-13, 0) * mm, "end": v(12, 0) * mm, "construction": true});
            skLineSegment(sketch, "E32.direction2", {"start": v(-13, 0) * mm, "end": v(-13, 10) * mm, "construction": true});
            const initialGuessF2  = {"E10": [-0.017, 0.01082, 0, -1, 0.002], "E11": [-0.015, 0.01943, 0, 1, 0.002], "E12": [-0.015, 0.0292, 0, 1, 0.002], "E13": [-0.015, 0.0392, 0, 1, 0.002], "E14": [-0.015, 0.04914, 0, 1, 0.002], "E15": [-0.015, 0.0592, 0, 1, 0.002], "E16": [-0.015, 0.069, 0, 1, 0.00247], "E17": [-0.015, 0.079, 0, 1, 0.00247], "E18": [-0.015, 0.089, 0, 1, 0.00247], "E19": [-0.015, 0.099, 0, 1, 0.00247], "E20": [-0.015, 0.10821, 0, 1, 0.00222], "E21": [-0.015, 0.11848, 0, 1, 0.00222], "E22": [-0.015, 0.12822, 0, 1, 0.00222], "E23": [-0.015, 0.13823, 0, 1, 0.00222]};
            skSetInitialGuess(sketch, initialGuessF2);
            skSolve(sketch);
        }
        {
            var Q0;
            Q0=qSketchRegion(id+"F2",true);
            extrude(context, id + "F3", {"entities" : qUnion([Q0]), "operationType" : NewBodyOperationType.ADD, "endBound" : BoundingType.SYMMETRIC, "oppositeDirection" : true, "depth" : 10 * mm, "offsetDistance" : 25 * mm});
        }
        {
            var Q0;
            Q0=qCreatedBy(makeId("Right.planeOp"),FACE);
            var sketch = newSketch(context, id + "F4", { "sketchPlane" : qUnion([Q0])});
            skLineSegment(sketch, "E33.bottom", {"start": v(26.29, 33.53) * mm, "end": v(34.29, 33.53) * mm});
            skLineSegment(sketch, "E33.top", {"start": v(26.29, 158.53) * mm, "end": v(34.29, 158.53) * mm});
            skLineSegment(sketch, "E33.left", {"start": v(26.29, 33.53) * mm, "end": v(26.29, 158.53) * mm});
            skLineSegment(sketch, "E33.right", {"start": v(34.29, 33.53) * mm, "end": v(34.29, 158.53) * mm});
            skSolve(sketch);
        }
        {
            var Q0;
            Q0 = qSketchRegion(id + "F4", true);
            extrude(context, id + "F5", {"entities" : qUnion([Q0]), "depth" : 0.4 * mm, "offsetDistance" : 25 * mm});
        }
        {
            var Q0;
            Q0=makeQuery(id+"F5.opExtrude","SWEPT_EDGE",EDGE,{"disambiguationData":[OSD([sQuery(id+"F4.wireOp",EDGE,"E33.top"),sQuery(id+"F4.wireOp",EDGE,"E33.left")])]});
            var Q1;
            Q1=makeQuery(id+"F5.opExtrude","SWEPT_EDGE",EDGE,{"disambiguationData":[OSD([sQuery(id+"F4.wireOp",EDGE,"E33.top"),sQuery(id+"F4.wireOp",EDGE,"E33.right")])]});
            var Q2;
            Q2=makeQuery(id+"F5.opExtrude","SWEPT_EDGE",EDGE,{"disambiguationData":[OSD([sQuery(id+"F4.wireOp",EDGE,"E33.bottom"),sQuery(id+"F4.wireOp",EDGE,"E33.right")])]});
            var Q3;
            Q3=makeQuery(id+"F5.opExtrude","SWEPT_EDGE",EDGE,{"disambiguationData":[OSD([sQuery(id+"F4.wireOp",EDGE,"E33.bottom"),sQuery(id+"F4.wireOp",EDGE,"E33.left")])]});
            fillet(context, id + "F6", {"entities" : qUnion([Q0, Q1, Q2, Q3]), "radius" : 2 * mm, "tangentPropagation" : true, "allowEdgeOverflow" : false});
        }
        {
            var Q0;
            Q0=makeQuery(id+"F5.opExtrude","CAP_FACE",FACE,{"disambiguationData":[OSD([sQuery(id+"F4.wireOp",EDGE,"E33.bottom"),sQuery(id+"F4.wireOp",EDGE,"E33.top"),sQuery(id+"F4.wireOp",EDGE,"E33.left"),sQuery(id+"F4.wireOp",EDGE,"E33.right")])],"isStart":false});
            var sketch = newSketch(context, id + "F7", { "sketchPlane" : qUnion([Q0])});
            skLineSegment(sketch, "E34", {"start": v(26.29, 135.36) * mm, "end": v(34.29, 135.36) * mm, "construction": true});
            skLineSegment(sketch, "E35", {"start": v(30.29, 152.58) * mm, "end": v(30.29, 95.45) * mm, "construction": true});
            skPoint(sketch, "E36", {"position": v(30.29, 135.36) * mm});
            skLineSegment(sketch, "E37.top", {"start": v(28.46, 115.03) * mm, "end": v(32.12, 115.03) * mm});
            skLineSegment(sketch, "E37.left", {"start": v(28.46, 133.53) * mm, "end": v(28.46, 115.03) * mm});
            skLineSegment(sketch, "E37.right", {"start": v(32.12, 133.53) * mm, "end": v(32.12, 115.03) * mm});
            skPoint(sketch, "E37.middle", {"position": v(30.29, 124.28) * mm});
            skArc(sketch, "E38", {"start": v(32.12, 133.53) * mm, "mid": v(30.29, 135.36) * mm, "end": v(28.46, 133.53) * mm});
            skSolve(sketch);
        }
        {
            var Q0;
            Q0 = qSketchRegion(id + "F7", true);
            extrude(context, id + "F8", {"entities" : qUnion([Q0]), "operationType" : NewBodyOperationType.REMOVE, "endBound" : BoundingType.SYMMETRIC, "oppositeDirection" : true, "depth" : 25 * mm, "offsetDistance" : 25 * mm});
        }
        {
            var Q0;
            Q0=makeQuery(id+"F1.opExtrude","SWEPT_BODY",BODY,{"disambiguationData":[OSD([sQuery(id+"F0.wireOp",EDGE,"E0.bottom"),sQuery(id+"F0.wireOp",EDGE,"E0.top"),sQuery(id+"F0.wireOp",EDGE,"E0.left"),sQuery(id+"F0.wireOp",EDGE,"E0.right")])]});
            transform(context, id + "F9", {"entities" : qUnion([Q0]), "transformType" : TransformType.TRANSLATION_3D, "dx" : 5.3 * mm, "dy" : 45 * mm, "dz" : 25 * mm, "makeCopy" : false});
        }
        {
            var Q0;
            {var subQ0=sQuery(id+"F0.wireOp",EDGE,"E0.top");var subQ1=sQuery(id+"F0.wireOp",EDGE,"E0.right");var subQ2=sQuery(id+"F0.wireOp",EDGE,"E0.bottom");var subQ3=sQuery(id+"F0.wireOp",EDGE,"E0.left");Q0=makeQuery(id+"F3.boolean.opBoolean","SPLIT",FACE,{"disambiguationData":[TD([makeQuery(id+"F1.opExtrude","SWEPT_FACE",FACE,{"disambiguationData":[OSD([subQ2])]})])],"derivedFrom":makeQuery(id+"F1.opExtrude","CAP_FACE",FACE,{"disambiguationData":[OSD([subQ2,subQ0,subQ3,subQ1])],"isStart":false})});}
            var sketch = newSketch(context, id + "F10", { "sketchPlane" : qUnion([Q0])});
            skLineSegment(sketch, "E39.bottom", {"start": v(6.31, 193.14) * mm, "end": v(49.94, 193.14) * mm});
            skLineSegment(sketch, "E39.top", {"start": v(6.31, 157.78) * mm, "end": v(49.94, 157.78) * mm});
            skLineSegment(sketch, "E39.left", {"start": v(6.31, 193.14) * mm, "end": v(6.31, 157.78) * mm});
            skLineSegment(sketch, "E39.right", {"start": v(49.94, 193.14) * mm, "end": v(49.94, 157.78) * mm});
            skLineSegment(sketch, "E40.bottom", {"start": v(54.17, 196.62) * mm, "end": v(32, 196.62) * mm});
            skLineSegment(sketch, "E40.top", {"start": v(54.17, 155.9) * mm, "end": v(32, 155.9) * mm});
            skLineSegment(sketch, "E40.left", {"start": v(54.17, 196.62) * mm, "end": v(54.17, 155.9) * mm});
            skLineSegment(sketch, "E40.right", {"start": v(32, 196.62) * mm, "end": v(32, 155.9) * mm});
            skSolve(sketch);
        }
        {
            var Q0;
            Q0 = qSketchRegion(id + "F10", true);
            extrude(context, id + "F11", {"entities" : qUnion([Q0]), "operationType" : NewBodyOperationType.REMOVE, "endBound" : BoundingType.SYMMETRIC, "oppositeDirection" : true, "depth" : 25 * mm, "offsetDistance" : 25 * mm});
        }
        {
            var Q0;
            Q0=makeQuery(id+"F1.opExtrude","SWEPT_BODY",BODY,{"disambiguationData":[OSD([sQuery(id+"F0.wireOp",EDGE,"E0.bottom"),sQuery(id+"F0.wireOp",EDGE,"E0.top"),sQuery(id+"F0.wireOp",EDGE,"E0.left"),sQuery(id+"F0.wireOp",EDGE,"E0.right")])]});
            var Q1;
            Q1=makeQuery(id+"F5.opExtrude","SWEPT_BODY",BODY,{"disambiguationData":[OSD([sQuery(id+"F4.wireOp",EDGE,"E33.bottom"),sQuery(id+"F4.wireOp",EDGE,"E33.top"),sQuery(id+"F4.wireOp",EDGE,"E33.left"),sQuery(id+"F4.wireOp",EDGE,"E33.right")])]});
            booleanBodies(context, id + "F12", {"operationType" : BooleanOperationType.SUBTRACTION, "tools" : qUnion([Q0]), "targets" : qUnion([Q1])});
        }
    });
